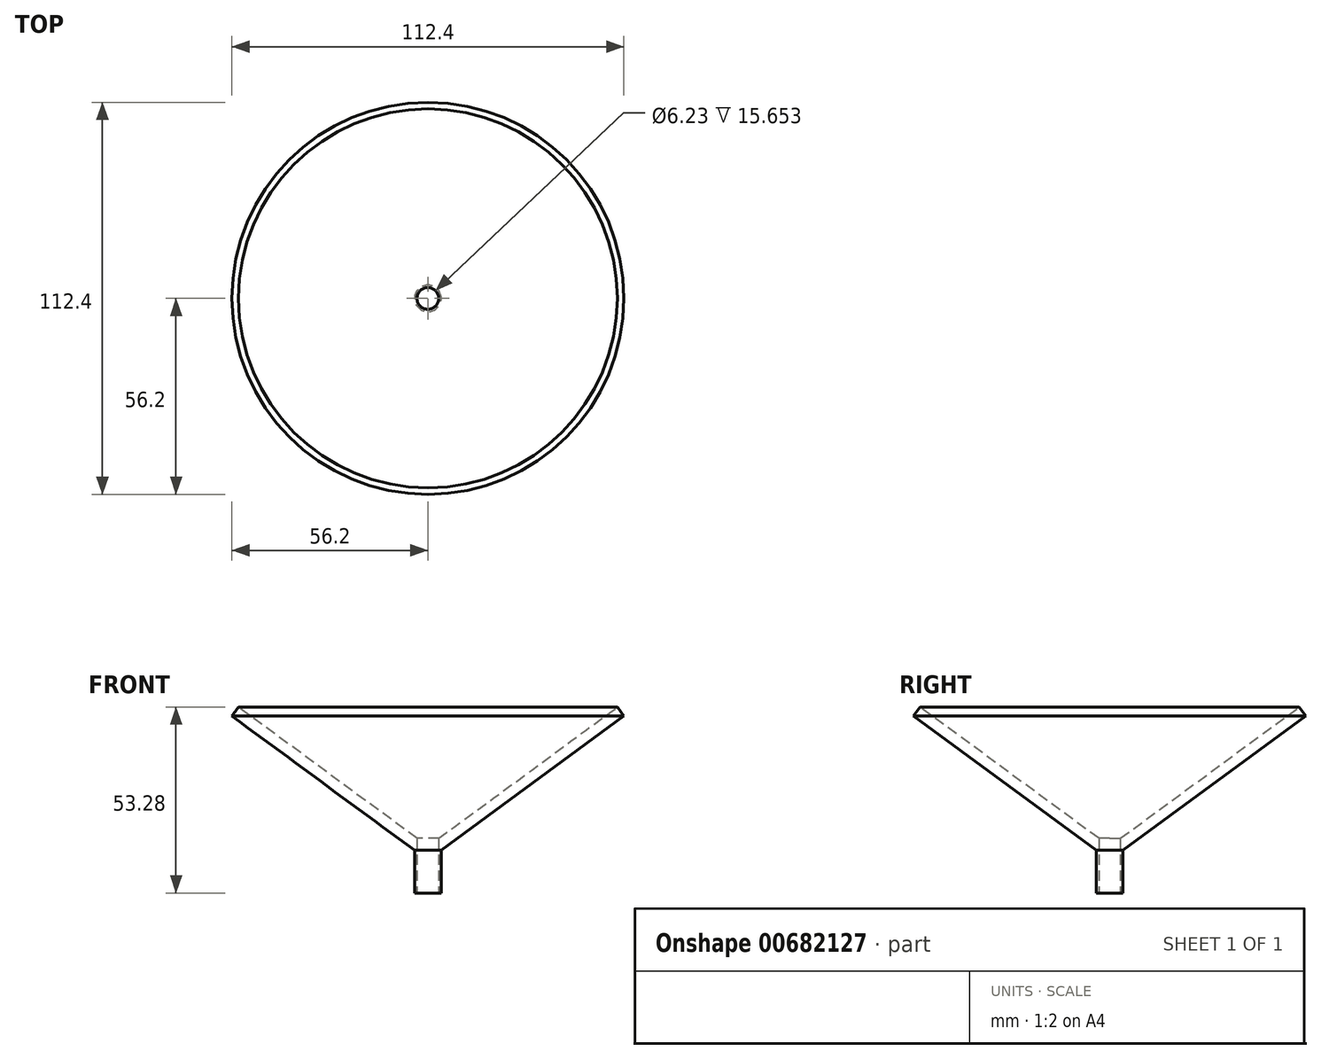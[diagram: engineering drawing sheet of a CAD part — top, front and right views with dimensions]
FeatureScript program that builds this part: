
annotation { "Feature Type Name" : "Feature", "Feature Type Description" : "" }
export const myFeature = defineFeature(function(context is Context, id is Id, definition is map)
    precondition{}
    {
        {
            var Q0;
            Q0=qCreatedBy(makeId("Front.planeOp"),FACE);
            var sketch = newSketch(context, id + "F0", { "sketchPlane" : qUnion([Q0])});
            skLineSegment(sketch, "E0", {"start": v(0, -21.1) * mm, "end": v(0, -9.26) * mm});
            skLineSegment(sketch, "E1", {"start": v(0, -9.26) * mm, "end": v(-54.33, 30.65) * mm});
            skLineSegment(sketch, "E2", {"start": v(-54.33, 30.65) * mm, "end": v(-56.2, 28.1) * mm});
            skLineSegment(sketch, "E3", {"start": v(-56.2, 28.1) * mm, "end": v(-3.8, -10.4) * mm});
            skLineSegment(sketch, "E4", {"start": v(-3.8, -10.4) * mm, "end": v(-3.8, -20.53) * mm});
            skLineSegment(sketch, "E5", {"start": v(-3.8, -20.53) * mm, "end": v(-3.8, -22.63) * mm});
            skLineSegment(sketch, "E6", {"start": v(-3.8, -22.63) * mm, "end": v(0, -22.63) * mm});
            skLineSegment(sketch, "E7", {"start": v(0, -21.1) * mm, "end": v(0, -22.63) * mm});
            skSolve(sketch);
        }
        {
            var Q0;
            Q0=makeQuery(id+"F0.imprint","IMPRINT",FACE,{"disambiguationData":[TD([[makeQuery(id+"F0.imprint","IMPRINT",EDGE,{"derivedFrom":sQuery(id+"F0.wireOp",EDGE,"E0")}),1.0]])]});
            var sketch = newSketch(context, id + "F1", { "sketchPlane" : qUnion([Q0])});
            skSolve(sketch);
        }
        {
            var Q0;
            Q0 = qSketchRegion(id + "F1", true);
            var Q1;
            Q1=makeQuery(id+"F0.imprint","IMPRINT",FACE,{"disambiguationData":[TD([[makeQuery(id+"F0.imprint","IMPRINT",EDGE,{"derivedFrom":sQuery(id+"F0.wireOp",EDGE,"E0")}),1.0]])]});
            var Q2;
            Q2=sQuery(id+"F0.wireOp",EDGE,"E0");
            revolve(context, id + "F2", {"entities" : qUnion([Q0, Q1]), "axis" : qUnion([Q2]), "revolveType" : RevolveType.FULL});
        }
        {
            var Q0;
            Q0=makeQuery(id+"F2.opRevolve","SWEPT_FACE",FACE,{"disambiguationData":[OSD([sQuery(id+"F0.wireOp",EDGE,"E6")])]});
            var sketch = newSketch(context, id + "F3", { "sketchPlane" : qUnion([Q0])});
            skCircle(sketch, "E8", {"center": v(0, 0) * mm, "radius": 3.11 * mm});
            skSolve(sketch);
        }
        {
            var Q0;
            Q0=makeQuery(id+"F3.imprint","IMPRINT",FACE,{"disambiguationData":[TD([[makeQuery(id+"F3.imprint","IMPRINT",EDGE,{"derivedFrom":sQuery(id+"F3.wireOp",EDGE,"E8")}),1.0]])]});
            var Q1;
            Q1=sQuery(id+"F3.wireOp",EDGE,"E8");
            extrude(context, id + "F4", {"entities" : qUnion([Q0]), "operationType" : NewBodyOperationType.REMOVE, "surfaceEntities" : qUnion([Q1]), "oppositeDirection" : true, "depth" : 25.4 * mm, "offsetDistance" : 25.4 * mm});
        }
    });
